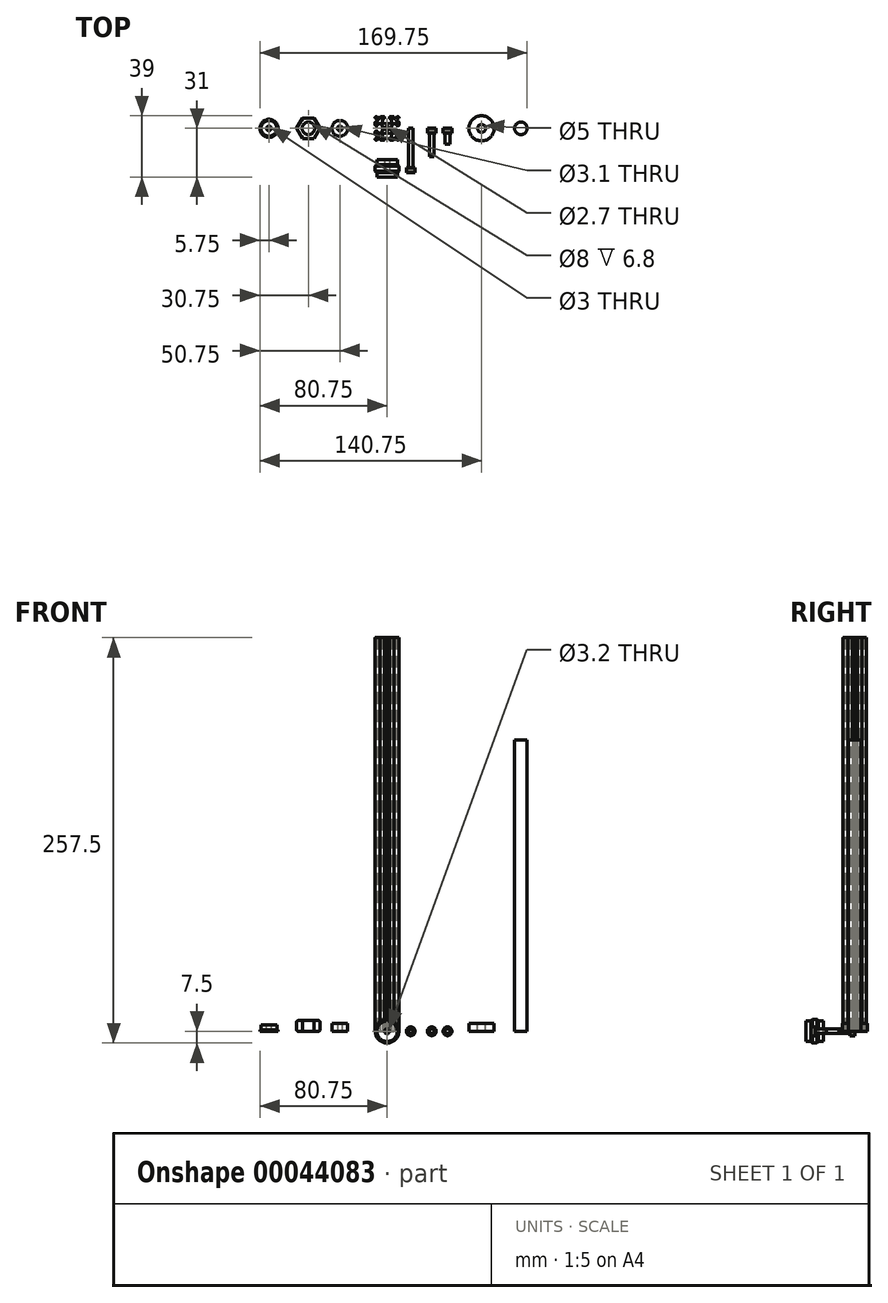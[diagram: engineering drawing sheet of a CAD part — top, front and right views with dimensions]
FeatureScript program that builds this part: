
annotation { "Feature Type Name" : "Feature", "Feature Type Description" : "" }
export const myFeature = defineFeature(function(context is Context, id is Id, definition is map)
    precondition{}
    {
        {
            var Q0;
            Q0=qCreatedBy(makeId("Top.planeOp"),FACE);
            var sketch = newSketch(context, id + "F0", { "sketchPlane" : qUnion([Q0])});
            skLineSegment(sketch, "E0", {"start": v(0, 0) * mm, "end": v(-7.5, -7.5) * mm, "construction": true});
            skArc(sketch, "E1", {"start": v(-1.35, 0) * mm, "mid": v(-1.25, -0.52) * mm, "end": v(-0.95, -0.95) * mm});
            skLineSegment(sketch, "E2", {"start": v(-7.5, -7) * mm, "end": v(-7.5, -6.72) * mm});
            skLineSegment(sketch, "E3", {"start": v(-7.35, -6.36) * mm, "end": v(-6.25, -5.26) * mm});
            skLineSegment(sketch, "E4", {"start": v(-6.6, -4.4) * mm, "end": v(-7, -4.4) * mm});
            skLineSegment(sketch, "E5", {"start": v(-7.5, -3.9) * mm, "end": v(-7.5, -2.1) * mm});
            skLineSegment(sketch, "E6", {"start": v(-7, -1.6) * mm, "end": v(-6.6, -1.6) * mm});
            skLineSegment(sketch, "E7", {"start": v(-6.1, -2.1) * mm, "end": v(-6.1, -2.7) * mm});
            skLineSegment(sketch, "E8", {"start": v(-5.9, -2.9) * mm, "end": v(-3.74, -2.9) * mm});
            skLineSegment(sketch, "E9", {"start": v(-3.25, -2.49) * mm, "end": v(-2.93, -0.73) * mm});
            skLineSegment(sketch, "E10", {"start": v(-2.73, -0.57) * mm, "end": v(-2.6, -0.57) * mm});
            skLineSegment(sketch, "E11", {"start": v(-2.4, -0.37) * mm, "end": v(-2.4, 0) * mm});
            skLineSegment(sketch, "E12", {"start": v(-2.4, 0) * mm, "end": v(-1.35, 0) * mm, "construction": true});
            skPoint(sketch, "E13.visualSharp", {"position": v(-5.4, -4.4) * mm});
            skArc(sketch, "E13.filletArc", {"start": v(-6.25, -5.26) * mm, "mid": v(-6.14, -4.71) * mm, "end": v(-6.6, -4.4) * mm});
            skPoint(sketch, "E14.visualSharp", {"position": v(-6.1, -2.9) * mm});
            skArc(sketch, "E14.filletArc", {"start": v(-6.1, -2.7) * mm, "mid": v(-6.04, -2.84) * mm, "end": v(-5.9, -2.9) * mm});
            skPoint(sketch, "E15.visualSharp", {"position": v(-6.1, -1.6) * mm});
            skArc(sketch, "E15.filletArc", {"start": v(-6.1, -2.1) * mm, "mid": v(-6.25, -1.75) * mm, "end": v(-6.6, -1.6) * mm});
            skPoint(sketch, "E16.visualSharp", {"position": v(-7.5, -1.6) * mm});
            skArc(sketch, "E16.filletArc", {"start": v(-7, -1.6) * mm, "mid": v(-7.35, -1.75) * mm, "end": v(-7.5, -2.1) * mm});
            skPoint(sketch, "E17.visualSharp", {"position": v(-7.5, -4.4) * mm});
            skArc(sketch, "E17.filletArc", {"start": v(-7.5, -3.9) * mm, "mid": v(-7.35, -4.26) * mm, "end": v(-7, -4.4) * mm});
            skPoint(sketch, "E18.visualSharp", {"position": v(-7.5, -6.51) * mm});
            skArc(sketch, "E18.filletArc", {"start": v(-7.35, -6.36) * mm, "mid": v(-7.46, -6.53) * mm, "end": v(-7.5, -6.72) * mm});
            skPoint(sketch, "E19.visualSharp", {"position": v(-3.32, -2.9) * mm});
            skArc(sketch, "E19.filletArc", {"start": v(-3.74, -2.9) * mm, "mid": v(-3.42, -2.78) * mm, "end": v(-3.25, -2.49) * mm});
            skPoint(sketch, "E20.visualSharp", {"position": v(-2.9, -0.57) * mm});
            skArc(sketch, "E20.filletArc", {"start": v(-2.73, -0.57) * mm, "mid": v(-2.86, -0.62) * mm, "end": v(-2.93, -0.73) * mm});
            skPoint(sketch, "E21.visualSharp", {"position": v(-2.4, -0.57) * mm});
            skArc(sketch, "E21.filletArc", {"start": v(-2.6, -0.57) * mm, "mid": v(-2.46, -0.51) * mm, "end": v(-2.4, -0.37) * mm});
            skLineSegment(sketch, "E22.0.MirrorCS", {"start": v(0, -2.4) * mm, "end": v(0, -1.35) * mm, "construction": true});
            skPoint(sketch, "E22.1.MirrorP", {"position": v(-4.4, -7.5) * mm});
            skArc(sketch, "E22.2.MirrorCS", {"start": v(-6.36, -7.35) * mm, "mid": v(-6.53, -7.46) * mm, "end": v(-6.72, -7.5) * mm});
            skPoint(sketch, "E22.3.MirrorP", {"position": v(-1.6, -7.5) * mm});
            skArc(sketch, "E22.4.MirrorCS", {"start": v(-1.6, -7) * mm, "mid": v(-1.75, -7.35) * mm, "end": v(-2.1, -7.5) * mm});
            skArc(sketch, "E22.5.MirrorCS", {"start": v(-0.57, -2.73) * mm, "mid": v(-0.62, -2.86) * mm, "end": v(-0.73, -2.93) * mm});
            skPoint(sketch, "E22.6.MirrorP", {"position": v(-1.6, -6.1) * mm});
            skLineSegment(sketch, "E22.7.MirrorCS", {"start": v(-3.9, -7.5) * mm, "end": v(-2.1, -7.5) * mm});
            skArc(sketch, "E22.8.MirrorCS", {"start": v(-5.26, -6.25) * mm, "mid": v(-4.71, -6.14) * mm, "end": v(-4.4, -6.6) * mm});
            skPoint(sketch, "E22.9.MirrorP", {"position": v(-0.57, -2.4) * mm});
            skPoint(sketch, "E22.10.MirrorP", {"position": v(-4.4, -5.4) * mm});
            skArc(sketch, "E22.11.MirrorCS", {"start": v(-2.7, -6.1) * mm, "mid": v(-2.84, -6.04) * mm, "end": v(-2.9, -5.9) * mm});
            skPoint(sketch, "E22.12.MirrorP", {"position": v(-0.57, -2.9) * mm});
            skLineSegment(sketch, "E22.13.MirrorCS", {"start": v(-7, -7.5) * mm, "end": v(-6.72, -7.5) * mm});
            skLineSegment(sketch, "E22.14.MirrorCS", {"start": v(-1.6, -7) * mm, "end": v(-1.6, -6.6) * mm});
            skLineSegment(sketch, "E22.15.MirrorCS", {"start": v(-6.36, -7.35) * mm, "end": v(-5.26, -6.25) * mm});
            skArc(sketch, "E22.16.MirrorCS", {"start": v(-2.1, -6.1) * mm, "mid": v(-1.75, -6.25) * mm, "end": v(-1.6, -6.6) * mm});
            skLineSegment(sketch, "E22.17.MirrorCS", {"start": v(-4.4, -6.6) * mm, "end": v(-4.4, -7) * mm});
            skArc(sketch, "E22.18.MirrorCS", {"start": v(-2.9, -3.74) * mm, "mid": v(-2.78, -3.42) * mm, "end": v(-2.49, -3.25) * mm});
            skLineSegment(sketch, "E22.19.MirrorCS", {"start": v(-2.9, -5.9) * mm, "end": v(-2.9, -3.74) * mm});
            skLineSegment(sketch, "E22.20.MirrorCS", {"start": v(-2.1, -6.1) * mm, "end": v(-2.7, -6.1) * mm});
            skArc(sketch, "E22.21.MirrorCS", {"start": v(-0.57, -2.6) * mm, "mid": v(-0.51, -2.46) * mm, "end": v(-0.37, -2.4) * mm});
            skLineSegment(sketch, "E22.22.MirrorCS", {"start": v(-0.37, -2.4) * mm, "end": v(0, -2.4) * mm});
            skPoint(sketch, "E22.23.MirrorP", {"position": v(-6.51, -7.5) * mm});
            skPoint(sketch, "E22.24.MirrorP", {"position": v(-2.9, -6.1) * mm});
            skLineSegment(sketch, "E22.25.MirrorCS", {"start": v(-2.49, -3.25) * mm, "end": v(-0.73, -2.93) * mm});
            skLineSegment(sketch, "E22.26.MirrorCS", {"start": v(-0.57, -2.73) * mm, "end": v(-0.57, -2.6) * mm});
            skArc(sketch, "E22.27.MirrorCS", {"start": v(0, -1.35) * mm, "mid": v(-0.52, -1.25) * mm, "end": v(-0.95, -0.95) * mm});
            skArc(sketch, "E22.28.MirrorCS", {"start": v(-3.9, -7.5) * mm, "mid": v(-4.26, -7.35) * mm, "end": v(-4.4, -7) * mm});
            skPoint(sketch, "E22.29.MirrorP", {"position": v(-2.9, -3.32) * mm});
            skPoint(sketch, "E23.visualSharp", {"position": v(-7.5, -7.5) * mm});
            skArc(sketch, "E23.filletArc", {"start": v(-7.5, -7) * mm, "mid": v(-7.35, -7.35) * mm, "end": v(-7, -7.5) * mm});
            skLineSegment(sketch, "E24.0.MirrorCS", {"start": v(0, 2.4) * mm, "end": v(0, 1.35) * mm, "construction": true});
            skLineSegment(sketch, "E24.1.MirrorCS", {"start": v(-2.1, 6.1) * mm, "end": v(-2.7, 6.1) * mm});
            skLineSegment(sketch, "E24.2.MirrorCS", {"start": v(-7.5, 3.9) * mm, "end": v(-7.5, 2.1) * mm});
            skLineSegment(sketch, "E24.3.MirrorCS", {"start": v(-7, 1.6) * mm, "end": v(-6.6, 1.6) * mm});
            skArc(sketch, "E24.4.MirrorCS", {"start": v(-6.1, 2.1) * mm, "mid": v(-6.25, 1.75) * mm, "end": v(-6.6, 1.6) * mm});
            skPoint(sketch, "E24.5.MirrorP", {"position": v(-3.32, 2.9) * mm});
            skPoint(sketch, "E24.6.MirrorP", {"position": v(-0.57, 2.9) * mm});
            skArc(sketch, "E24.7.MirrorCS", {"start": v(-0.57, 2.6) * mm, "mid": v(-0.51, 2.46) * mm, "end": v(-0.37, 2.4) * mm});
            skArc(sketch, "E24.8.MirrorCS", {"start": v(-2.6, 0.57) * mm, "mid": v(-2.46, 0.51) * mm, "end": v(-2.4, 0.37) * mm});
            skLineSegment(sketch, "E24.9.MirrorCS", {"start": v(-0.37, 2.4) * mm, "end": v(0, 2.4) * mm});
            skArc(sketch, "E24.10.MirrorCS", {"start": v(-6.1, 2.7) * mm, "mid": v(-6.04, 2.84) * mm, "end": v(-5.9, 2.9) * mm});
            skPoint(sketch, "E24.11.MirrorP", {"position": v(-4.4, 5.4) * mm});
            skLineSegment(sketch, "E24.12.MirrorCS", {"start": v(-2.9, 5.9) * mm, "end": v(-2.9, 3.74) * mm});
            skLineSegment(sketch, "E24.13.MirrorCS", {"start": v(-7.35, 6.36) * mm, "end": v(-6.25, 5.26) * mm});
            skPoint(sketch, "E24.14.MirrorP", {"position": v(-7.5, 6.51) * mm});
            skArc(sketch, "E24.15.MirrorCS", {"start": v(-3.74, 2.9) * mm, "mid": v(-3.42, 2.78) * mm, "end": v(-3.25, 2.49) * mm});
            skArc(sketch, "E24.16.MirrorCS", {"start": v(-2.1, 6.1) * mm, "mid": v(-1.75, 6.25) * mm, "end": v(-1.6, 6.6) * mm});
            skArc(sketch, "E24.17.MirrorCS", {"start": v(-7, 1.6) * mm, "mid": v(-7.35, 1.75) * mm, "end": v(-7.5, 2.1) * mm});
            skPoint(sketch, "E24.18.MirrorP", {"position": v(-1.6, 6.1) * mm});
            skPoint(sketch, "E24.19.MirrorP", {"position": v(-7.5, 4.4) * mm});
            skLineSegment(sketch, "E24.20.MirrorCS", {"start": v(-4.4, 6.6) * mm, "end": v(-4.4, 7) * mm});
            skArc(sketch, "E24.21.MirrorCS", {"start": v(-7.5, 3.9) * mm, "mid": v(-7.35, 4.26) * mm, "end": v(-7, 4.4) * mm});
            skPoint(sketch, "E24.22.MirrorP", {"position": v(-0.57, 2.4) * mm});
            skLineSegment(sketch, "E24.23.MirrorCS", {"start": v(-5.9, 2.9) * mm, "end": v(-3.74, 2.9) * mm});
            skArc(sketch, "E24.24.MirrorCS", {"start": v(-2.9, 3.74) * mm, "mid": v(-2.78, 3.42) * mm, "end": v(-2.49, 3.25) * mm});
            skArc(sketch, "E24.25.MirrorCS", {"start": v(-7.35, 6.36) * mm, "mid": v(-7.46, 6.53) * mm, "end": v(-7.5, 6.72) * mm});
            skPoint(sketch, "E24.26.MirrorP", {"position": v(-6.1, 2.9) * mm});
            skPoint(sketch, "E24.27.MirrorP", {"position": v(-4.4, 7.5) * mm});
            skArc(sketch, "E24.28.MirrorCS", {"start": v(-5.26, 6.25) * mm, "mid": v(-4.71, 6.14) * mm, "end": v(-4.4, 6.6) * mm});
            skArc(sketch, "E24.29.MirrorCS", {"start": v(-7.5, 7) * mm, "mid": v(-7.35, 7.35) * mm, "end": v(-7, 7.5) * mm});
            skPoint(sketch, "E24.30.MirrorP", {"position": v(-6.1, 1.6) * mm});
            skPoint(sketch, "E24.31.MirrorP", {"position": v(-2.9, 3.32) * mm});
            skPoint(sketch, "E24.32.MirrorP", {"position": v(-1.6, 7.5) * mm});
            skPoint(sketch, "E24.33.MirrorP", {"position": v(-2.9, 6.1) * mm});
            skLineSegment(sketch, "E24.34.MirrorCS", {"start": v(-3.9, 7.5) * mm, "end": v(-2.1, 7.5) * mm});
            skLineSegment(sketch, "E24.35.MirrorCS", {"start": v(-7, 7.5) * mm, "end": v(-6.72, 7.5) * mm});
            skArc(sketch, "E24.36.MirrorCS", {"start": v(-3.9, 7.5) * mm, "mid": v(-4.26, 7.35) * mm, "end": v(-4.4, 7) * mm});
            skPoint(sketch, "E24.37.MirrorP", {"position": v(-7.5, 7.5) * mm});
            skLineSegment(sketch, "E24.38.MirrorCS", {"start": v(-1.6, 7) * mm, "end": v(-1.6, 6.6) * mm});
            skLineSegment(sketch, "E24.39.MirrorCS", {"start": v(-6.36, 7.35) * mm, "end": v(-5.26, 6.25) * mm});
            skPoint(sketch, "E24.40.MirrorP", {"position": v(-7.5, 1.6) * mm});
            skArc(sketch, "E24.41.MirrorCS", {"start": v(-2.7, 6.1) * mm, "mid": v(-2.84, 6.04) * mm, "end": v(-2.9, 5.9) * mm});
            skArc(sketch, "E24.42.MirrorCS", {"start": v(-6.36, 7.35) * mm, "mid": v(-6.53, 7.46) * mm, "end": v(-6.72, 7.5) * mm});
            skLineSegment(sketch, "E24.43.MirrorCS", {"start": v(-2.49, 3.25) * mm, "end": v(-0.73, 2.93) * mm});
            skPoint(sketch, "E24.44.MirrorP", {"position": v(-2.9, 0.57) * mm});
            skLineSegment(sketch, "E24.45.MirrorCS", {"start": v(-6.6, 4.4) * mm, "end": v(-7, 4.4) * mm});
            skArc(sketch, "E24.46.MirrorCS", {"start": v(-1.6, 7) * mm, "mid": v(-1.75, 7.35) * mm, "end": v(-2.1, 7.5) * mm});
            skArc(sketch, "E24.47.MirrorCS", {"start": v(-2.73, 0.57) * mm, "mid": v(-2.86, 0.62) * mm, "end": v(-2.93, 0.73) * mm});
            skArc(sketch, "E24.48.MirrorCS", {"start": v(-6.25, 5.26) * mm, "mid": v(-6.14, 4.71) * mm, "end": v(-6.6, 4.4) * mm});
            skLineSegment(sketch, "E24.49.MirrorCS", {"start": v(-0.57, 2.73) * mm, "end": v(-0.57, 2.6) * mm});
            skLineSegment(sketch, "E24.50.MirrorCS", {"start": v(-2.73, 0.57) * mm, "end": v(-2.6, 0.57) * mm});
            skArc(sketch, "E24.51.MirrorCS", {"start": v(-1.35, 0) * mm, "mid": v(-1.25, 0.52) * mm, "end": v(-0.95, 0.95) * mm});
            skPoint(sketch, "E24.52.MirrorP", {"position": v(-2.4, 0.57) * mm});
            skPoint(sketch, "E24.53.MirrorP", {"position": v(-5.4, 4.4) * mm});
            skLineSegment(sketch, "E24.54.MirrorCS", {"start": v(-2.4, 0.37) * mm, "end": v(-2.4, 0) * mm});
            skArc(sketch, "E24.55.MirrorCS", {"start": v(0, 1.35) * mm, "mid": v(-0.52, 1.25) * mm, "end": v(-0.95, 0.95) * mm});
            skLineSegment(sketch, "E24.56.MirrorCS", {"start": v(-3.25, 2.49) * mm, "end": v(-2.93, 0.73) * mm});
            skLineSegment(sketch, "E24.57.MirrorCS", {"start": v(-6.1, 2.1) * mm, "end": v(-6.1, 2.7) * mm});
            skLineSegment(sketch, "E24.58.MirrorCS", {"start": v(-7.5, 7) * mm, "end": v(-7.5, 6.72) * mm});
            skArc(sketch, "E24.59.MirrorCS", {"start": v(-0.57, 2.73) * mm, "mid": v(-0.62, 2.86) * mm, "end": v(-0.73, 2.93) * mm});
            skPoint(sketch, "E24.60.MirrorP", {"position": v(-6.51, 7.5) * mm});
            skLineSegment(sketch, "E25.0.MirrorCS", {"start": v(7, -7.5) * mm, "end": v(6.72, -7.5) * mm});
            skLineSegment(sketch, "E25.1.MirrorCS", {"start": v(0.57, 2.73) * mm, "end": v(0.57, 2.6) * mm});
            skLineSegment(sketch, "E25.2.MirrorCS", {"start": v(0.37, 2.4) * mm, "end": v(0, 2.4) * mm});
            skLineSegment(sketch, "E25.3.MirrorCS", {"start": v(7, 7.5) * mm, "end": v(6.72, 7.5) * mm});
            skLineSegment(sketch, "E25.4.MirrorCS", {"start": v(1.6, -7) * mm, "end": v(1.6, -6.6) * mm});
            skLineSegment(sketch, "E25.5.MirrorCS", {"start": v(2.73, 0.57) * mm, "end": v(2.6, 0.57) * mm});
            skLineSegment(sketch, "E25.6.MirrorCS", {"start": v(7, 1.6) * mm, "end": v(6.6, 1.6) * mm});
            skLineSegment(sketch, "E25.7.MirrorCS", {"start": v(5.9, 2.9) * mm, "end": v(3.74, 2.9) * mm});
            skLineSegment(sketch, "E25.8.MirrorCS", {"start": v(7.35, 6.36) * mm, "end": v(6.25, 5.26) * mm});
            skArc(sketch, "E25.9.MirrorCS", {"start": v(2.7, -6.1) * mm, "mid": v(2.84, -6.04) * mm, "end": v(2.9, -5.9) * mm});
            skArc(sketch, "E25.10.MirrorCS", {"start": v(2.9, 3.74) * mm, "mid": v(2.78, 3.42) * mm, "end": v(2.49, 3.25) * mm});
            skPoint(sketch, "E25.11.MirrorP", {"position": v(1.6, -7.5) * mm});
            skPoint(sketch, "E25.12.MirrorP", {"position": v(6.1, -1.6) * mm});
            skPoint(sketch, "E25.13.MirrorP", {"position": v(2.9, 3.32) * mm});
            skPoint(sketch, "E25.14.MirrorP", {"position": v(7.5, -1.6) * mm});
            skArc(sketch, "E25.15.MirrorCS", {"start": v(1.6, 7) * mm, "mid": v(1.75, 7.35) * mm, "end": v(2.1, 7.5) * mm});
            skLineSegment(sketch, "E25.16.MirrorCS", {"start": v(6.1, -2.1) * mm, "end": v(6.1, -2.7) * mm});
            skLineSegment(sketch, "E25.17.MirrorCS", {"start": v(2.4, 0.37) * mm, "end": v(2.4, 0) * mm});
            skArc(sketch, "E25.18.MirrorCS", {"start": v(7, -1.6) * mm, "mid": v(7.35, -1.75) * mm, "end": v(7.5, -2.1) * mm});
            skArc(sketch, "E25.19.MirrorCS", {"start": v(7.5, 7) * mm, "mid": v(7.35, 7.35) * mm, "end": v(7, 7.5) * mm});
            skArc(sketch, "E25.20.MirrorCS", {"start": v(2.1, -6.1) * mm, "mid": v(1.75, -6.25) * mm, "end": v(1.6, -6.6) * mm});
            skArc(sketch, "E25.21.MirrorCS", {"start": v(6.1, 2.1) * mm, "mid": v(6.25, 1.75) * mm, "end": v(6.6, 1.6) * mm});
            skLineSegment(sketch, "E25.22.MirrorCS", {"start": v(4.4, 6.6) * mm, "end": v(4.4, 7) * mm});
            skLineSegment(sketch, "E25.23.MirrorCS", {"start": v(6.6, 4.4) * mm, "end": v(7, 4.4) * mm});
            skArc(sketch, "E25.24.MirrorCS", {"start": v(7, 1.6) * mm, "mid": v(7.35, 1.75) * mm, "end": v(7.5, 2.1) * mm});
            skArc(sketch, "E25.25.MirrorCS", {"start": v(0, -1.35) * mm, "mid": v(0.52, -1.25) * mm, "end": v(0.95, -0.95) * mm});
            skLineSegment(sketch, "E25.26.MirrorCS", {"start": v(3.9, -7.5) * mm, "end": v(2.1, -7.5) * mm});
            skLineSegment(sketch, "E25.27.MirrorCS", {"start": v(2.1, 6.1) * mm, "end": v(2.7, 6.1) * mm});
            skLineSegment(sketch, "E25.28.MirrorCS", {"start": v(2.73, -0.57) * mm, "end": v(2.6, -0.57) * mm});
            skLineSegment(sketch, "E25.29.MirrorCS", {"start": v(4.4, -6.6) * mm, "end": v(4.4, -7) * mm});
            skLineSegment(sketch, "E25.30.MirrorCS", {"start": v(3.9, 7.5) * mm, "end": v(2.1, 7.5) * mm});
            skArc(sketch, "E25.31.MirrorCS", {"start": v(0.57, -2.73) * mm, "mid": v(0.62, -2.86) * mm, "end": v(0.73, -2.93) * mm});
            skArc(sketch, "E25.32.MirrorCS", {"start": v(0.57, 2.6) * mm, "mid": v(0.51, 2.46) * mm, "end": v(0.37, 2.4) * mm});
            skPoint(sketch, "E25.33.MirrorP", {"position": v(6.51, -7.5) * mm});
            skArc(sketch, "E25.34.MirrorCS", {"start": v(3.9, -7.5) * mm, "mid": v(4.26, -7.35) * mm, "end": v(4.4, -7) * mm});
            skArc(sketch, "E25.35.MirrorCS", {"start": v(2.7, 6.1) * mm, "mid": v(2.84, 6.04) * mm, "end": v(2.9, 5.9) * mm});
            skPoint(sketch, "E25.36.MirrorP", {"position": v(0.57, -2.4) * mm});
            skPoint(sketch, "E25.37.MirrorP", {"position": v(0.57, 2.9) * mm});
            skLineSegment(sketch, "E25.38.MirrorCS", {"start": v(3.25, -2.49) * mm, "end": v(2.93, -0.73) * mm});
            skPoint(sketch, "E25.39.MirrorP", {"position": v(5.4, -4.4) * mm});
            skPoint(sketch, "E25.40.MirrorP", {"position": v(2.4, -0.57) * mm});
            skLineSegment(sketch, "E25.41.MirrorCS", {"start": v(7.5, -7) * mm, "end": v(7.5, -6.72) * mm});
            skArc(sketch, "E25.42.MirrorCS", {"start": v(7.35, 6.36) * mm, "mid": v(7.46, 6.53) * mm, "end": v(7.5, 6.72) * mm});
            skPoint(sketch, "E25.43.MirrorP", {"position": v(4.4, 7.5) * mm});
            skArc(sketch, "E25.44.MirrorCS", {"start": v(6.25, 5.26) * mm, "mid": v(6.14, 4.71) * mm, "end": v(6.6, 4.4) * mm});
            skPoint(sketch, "E25.45.MirrorP", {"position": v(6.1, -2.9) * mm});
            skPoint(sketch, "E25.46.MirrorP", {"position": v(4.4, -7.5) * mm});
            skArc(sketch, "E25.47.MirrorCS", {"start": v(6.1, 2.7) * mm, "mid": v(6.04, 2.84) * mm, "end": v(5.9, 2.9) * mm});
            skLineSegment(sketch, "E25.48.MirrorCS", {"start": v(2.1, -6.1) * mm, "end": v(2.7, -6.1) * mm});
            skArc(sketch, "E25.49.MirrorCS", {"start": v(2.73, -0.57) * mm, "mid": v(2.86, -0.62) * mm, "end": v(2.93, -0.73) * mm});
            skArc(sketch, "E25.50.MirrorCS", {"start": v(7.35, -6.36) * mm, "mid": v(7.46, -6.53) * mm, "end": v(7.5, -6.72) * mm});
            skLineSegment(sketch, "E25.51.MirrorCS", {"start": v(3.25, 2.49) * mm, "end": v(2.93, 0.73) * mm});
            skArc(sketch, "E25.52.MirrorCS", {"start": v(2.9, -3.74) * mm, "mid": v(2.78, -3.42) * mm, "end": v(2.49, -3.25) * mm});
            skArc(sketch, "E25.53.MirrorCS", {"start": v(2.6, 0.57) * mm, "mid": v(2.46, 0.51) * mm, "end": v(2.4, 0.37) * mm});
            skPoint(sketch, "E25.54.MirrorP", {"position": v(2.9, 0.57) * mm});
            skPoint(sketch, "E25.55.MirrorP", {"position": v(7.5, -6.51) * mm});
            skLineSegment(sketch, "E25.56.MirrorCS", {"start": v(2.49, 3.25) * mm, "end": v(0.73, 2.93) * mm});
            skArc(sketch, "E25.57.MirrorCS", {"start": v(1.6, -7) * mm, "mid": v(1.75, -7.35) * mm, "end": v(2.1, -7.5) * mm});
            skArc(sketch, "E25.58.MirrorCS", {"start": v(2.1, 6.1) * mm, "mid": v(1.75, 6.25) * mm, "end": v(1.6, 6.6) * mm});
            skLineSegment(sketch, "E25.59.MirrorCS", {"start": v(0.57, -2.73) * mm, "end": v(0.57, -2.6) * mm});
            skLineSegment(sketch, "E25.60.MirrorCS", {"start": v(2.4, -0.37) * mm, "end": v(2.4, 0) * mm});
            skArc(sketch, "E25.61.MirrorCS", {"start": v(7.5, -3.9) * mm, "mid": v(7.35, -4.26) * mm, "end": v(7, -4.4) * mm});
            skLineSegment(sketch, "E25.62.MirrorCS", {"start": v(5.9, -2.9) * mm, "end": v(3.74, -2.9) * mm});
            skLineSegment(sketch, "E25.63.MirrorCS", {"start": v(7.5, -3.9) * mm, "end": v(7.5, -2.1) * mm});
            skLineSegment(sketch, "E25.64.MirrorCS", {"start": v(7, -1.6) * mm, "end": v(6.6, -1.6) * mm});
            skArc(sketch, "E25.65.MirrorCS", {"start": v(1.35, 0) * mm, "mid": v(1.25, -0.52) * mm, "end": v(0.95, -0.95) * mm});
            skPoint(sketch, "E25.66.MirrorP", {"position": v(7.5, 1.6) * mm});
            skPoint(sketch, "E25.67.MirrorP", {"position": v(1.6, 6.1) * mm});
            skLineSegment(sketch, "E25.68.MirrorCS", {"start": v(6.36, -7.35) * mm, "end": v(5.26, -6.25) * mm});
            skPoint(sketch, "E25.69.MirrorP", {"position": v(2.4, 0.57) * mm});
            skPoint(sketch, "E25.70.MirrorP", {"position": v(6.1, 1.6) * mm});
            skPoint(sketch, "E25.71.MirrorP", {"position": v(3.32, -2.9) * mm});
            skPoint(sketch, "E25.72.MirrorP", {"position": v(0.57, -2.9) * mm});
            skPoint(sketch, "E25.73.MirrorP", {"position": v(7.5, 4.4) * mm});
            skArc(sketch, "E25.74.MirrorCS", {"start": v(5.26, -6.25) * mm, "mid": v(4.71, -6.14) * mm, "end": v(4.4, -6.6) * mm});
            skArc(sketch, "E25.75.MirrorCS", {"start": v(7.5, -7) * mm, "mid": v(7.35, -7.35) * mm, "end": v(7, -7.5) * mm});
            skLineSegment(sketch, "E25.76.MirrorCS", {"start": v(2.49, -3.25) * mm, "end": v(0.73, -2.93) * mm});
            skArc(sketch, "E25.77.MirrorCS", {"start": v(3.74, 2.9) * mm, "mid": v(3.42, 2.78) * mm, "end": v(3.25, 2.49) * mm});
            skArc(sketch, "E25.78.MirrorCS", {"start": v(6.36, -7.35) * mm, "mid": v(6.53, -7.46) * mm, "end": v(6.72, -7.5) * mm});
            skArc(sketch, "E25.79.MirrorCS", {"start": v(7.5, 3.9) * mm, "mid": v(7.35, 4.26) * mm, "end": v(7, 4.4) * mm});
            skArc(sketch, "E25.80.MirrorCS", {"start": v(2.73, 0.57) * mm, "mid": v(2.86, 0.62) * mm, "end": v(2.93, 0.73) * mm});
            skArc(sketch, "E25.81.MirrorCS", {"start": v(6.36, 7.35) * mm, "mid": v(6.53, 7.46) * mm, "end": v(6.72, 7.5) * mm});
            skPoint(sketch, "E25.82.MirrorP", {"position": v(4.4, -5.4) * mm});
            skPoint(sketch, "E25.83.MirrorP", {"position": v(6.51, 7.5) * mm});
            skPoint(sketch, "E25.84.MirrorP", {"position": v(2.9, -0.57) * mm});
            skLineSegment(sketch, "E25.85.MirrorCS", {"start": v(2.9, -5.9) * mm, "end": v(2.9, -3.74) * mm});
            skLineSegment(sketch, "E25.86.MirrorCS", {"start": v(6.1, 2.1) * mm, "end": v(6.1, 2.7) * mm});
            skLineSegment(sketch, "E25.87.MirrorCS", {"start": v(6.36, 7.35) * mm, "end": v(5.26, 6.25) * mm});
            skArc(sketch, "E25.88.MirrorCS", {"start": v(0.57, 2.73) * mm, "mid": v(0.62, 2.86) * mm, "end": v(0.73, 2.93) * mm});
            skArc(sketch, "E25.89.MirrorCS", {"start": v(0.57, -2.6) * mm, "mid": v(0.51, -2.46) * mm, "end": v(0.37, -2.4) * mm});
            skLineSegment(sketch, "E25.90.MirrorCS", {"start": v(2.9, 5.9) * mm, "end": v(2.9, 3.74) * mm});
            skArc(sketch, "E25.91.MirrorCS", {"start": v(0, 1.35) * mm, "mid": v(0.52, 1.25) * mm, "end": v(0.95, 0.95) * mm});
            skArc(sketch, "E25.92.MirrorCS", {"start": v(2.6, -0.57) * mm, "mid": v(2.46, -0.51) * mm, "end": v(2.4, -0.37) * mm});
            skPoint(sketch, "E25.93.MirrorP", {"position": v(4.4, 5.4) * mm});
            skPoint(sketch, "E25.94.MirrorP", {"position": v(2.9, -3.32) * mm});
            skPoint(sketch, "E25.95.MirrorP", {"position": v(2.9, 6.1) * mm});
            skPoint(sketch, "E25.96.MirrorP", {"position": v(5.4, 4.4) * mm});
            skPoint(sketch, "E25.97.MirrorP", {"position": v(3.32, 2.9) * mm});
            skArc(sketch, "E25.98.MirrorCS", {"start": v(3.74, -2.9) * mm, "mid": v(3.42, -2.78) * mm, "end": v(3.25, -2.49) * mm});
            skArc(sketch, "E25.99.MirrorCS", {"start": v(3.9, 7.5) * mm, "mid": v(4.26, 7.35) * mm, "end": v(4.4, 7) * mm});
            skPoint(sketch, "E25.100.MirrorP", {"position": v(7.5, -4.4) * mm});
            skPoint(sketch, "E25.101.MirrorP", {"position": v(6.1, 2.9) * mm});
            skArc(sketch, "E25.102.MirrorCS", {"start": v(1.35, 0) * mm, "mid": v(1.25, 0.52) * mm, "end": v(0.95, 0.95) * mm});
            skArc(sketch, "E25.103.MirrorCS", {"start": v(5.26, 6.25) * mm, "mid": v(4.71, 6.14) * mm, "end": v(4.4, 6.6) * mm});
            skPoint(sketch, "E25.104.MirrorP", {"position": v(7.5, 6.51) * mm});
            skPoint(sketch, "E25.105.MirrorP", {"position": v(2.9, -6.1) * mm});
            skArc(sketch, "E25.106.MirrorCS", {"start": v(6.25, -5.26) * mm, "mid": v(6.14, -4.71) * mm, "end": v(6.6, -4.4) * mm});
            skArc(sketch, "E25.107.MirrorCS", {"start": v(6.1, -2.1) * mm, "mid": v(6.25, -1.75) * mm, "end": v(6.6, -1.6) * mm});
            skPoint(sketch, "E25.108.MirrorP", {"position": v(1.6, 7.5) * mm});
            skPoint(sketch, "E25.109.MirrorP", {"position": v(7.5, 7.5) * mm});
            skLineSegment(sketch, "E25.110.MirrorCS", {"start": v(0.37, -2.4) * mm, "end": v(0, -2.4) * mm});
            skPoint(sketch, "E25.111.MirrorP", {"position": v(7.5, -7.5) * mm});
            skLineSegment(sketch, "E25.112.MirrorCS", {"start": v(7.5, 7) * mm, "end": v(7.5, 6.72) * mm});
            skArc(sketch, "E25.113.MirrorCS", {"start": v(6.1, -2.7) * mm, "mid": v(6.04, -2.84) * mm, "end": v(5.9, -2.9) * mm});
            skLineSegment(sketch, "E25.114.MirrorCS", {"start": v(1.6, 7) * mm, "end": v(1.6, 6.6) * mm});
            skPoint(sketch, "E25.115.MirrorP", {"position": v(1.6, -6.1) * mm});
            skLineSegment(sketch, "E25.116.MirrorCS", {"start": v(7.35, -6.36) * mm, "end": v(6.25, -5.26) * mm});
            skLineSegment(sketch, "E25.117.MirrorCS", {"start": v(7.5, 3.9) * mm, "end": v(7.5, 2.1) * mm});
            skPoint(sketch, "E25.118.MirrorP", {"position": v(0.57, 2.4) * mm});
            skLineSegment(sketch, "E25.119.MirrorCS", {"start": v(6.6, -4.4) * mm, "end": v(7, -4.4) * mm});
            skSolve(sketch);
        }
        {
            var Q0;
            Q0=makeQuery(id+"F0.imprint","IMPRINT",FACE,{"disambiguationData":[TD([[makeQuery(id+"F0.imprint","IMPRINT",EDGE,{"derivedFrom":sQuery(id+"F0.wireOp",EDGE,"E1")}),-1.0]])]});
            extrude(context, id + "F1", {"entities" : qUnion([Q0]), "depth" : 250 * mm});
        }
        {
            var Q0;
            Q0=qCreatedBy(makeId("Right.planeOp"),FACE);
            var sketch = newSketch(context, id + "F2", { "sketchPlane" : qUnion([Q0])});
            skLineSegment(sketch, "E26", {"start": v(-31, 0) * mm, "end": v(-31, 6.5) * mm});
            skLineSegment(sketch, "E27", {"start": v(-20, 6.5) * mm, "end": v(-20, 0) * mm});
            skLineSegment(sketch, "E28", {"start": v(-20, 0) * mm, "end": v(-31, 0) * mm});
            skLineSegment(sketch, "E29", {"start": v(-31, 6.5) * mm, "end": v(-28, 6.5) * mm});
            skLineSegment(sketch, "E30", {"start": v(-28, 6.5) * mm, "end": v(-27, 7.5) * mm});
            skLineSegment(sketch, "E31", {"start": v(-27, 7.5) * mm, "end": v(-24, 7.5) * mm});
            skLineSegment(sketch, "E32", {"start": v(-24, 7.5) * mm, "end": v(-23, 6.5) * mm});
            skLineSegment(sketch, "E33", {"start": v(-23, 6.5) * mm, "end": v(-20, 6.5) * mm});
            skLineSegment(sketch, "E34", {"start": v(-25.5, 7.5) * mm, "end": v(-25.5, 0) * mm, "construction": true});
            skSolve(sketch);
        }
        {
            var Q0;
            Q0 = qSketchRegion(id + "F2", true);
            var Q1;
            Q1=sQuery(id+"F2.wireOp",EDGE,"E28");
            revolve(context, id + "F3", {"entities" : qUnion([Q0]), "axis" : qUnion([Q1]), "revolveType" : RevolveType.FULL});
        }
        {
            var Q0;
            Q0=makeQuery(id+"F3.opRevolve","SWEPT_FACE",FACE,{"disambiguationData":[OSD([sQuery(id+"F2.wireOp",EDGE,"E26")])]});
            var sketch = newSketch(context, id + "F4", { "sketchPlane" : qUnion([Q0])});
            skCircle(sketch, "E35", {"center": v(0, 0) * mm, "radius": 1.6 * mm});
            skSolve(sketch);
        }
        {
            var Q0;
            Q0=makeQuery(id+"F4.imprint","IMPRINT",FACE,{"disambiguationData":[TD([[makeQuery(id+"F4.imprint","IMPRINT",EDGE,{"derivedFrom":sQuery(id+"F4.wireOp",EDGE,"E35")}),1.0]])]});
            extrude(context, id + "F5", {"entities" : qUnion([Q0]), "operationType" : NewBodyOperationType.REMOVE, "oppositeDirection" : true, "depth" : 11 * mm});
        }
        {
            var Q0;
            Q0=qCreatedBy(makeId("Front.planeOp"),FACE);
            var sketch = newSketch(context, id + "F6", { "sketchPlane" : qUnion([Q0])});
            skCircle(sketch, "E36", {"center": v(15, 0) * mm, "radius": 1.5 * mm});
            skSolve(sketch);
        }
        {
            var Q0;
            Q0=makeQuery(id+"F6.imprint","IMPRINT",FACE,{"disambiguationData":[TD([[makeQuery(id+"F6.imprint","IMPRINT",EDGE,{"derivedFrom":sQuery(id+"F6.wireOp",EDGE,"E36")}),1.0]])]});
            extrude(context, id + "F7", {"entities" : qUnion([Q0]), "depth" : 25 * mm});
        }
        {
            var Q0;
            Q0=makeQuery(id+"F7.opExtrude","CAP_FACE",FACE,{"disambiguationData":[OSD([sQuery(id+"F6.wireOp",EDGE,"E36")])],"isStart":false});
            var sketch = newSketch(context, id + "F8", { "sketchPlane" : qUnion([Q0])});
            skCircle(sketch, "E37", {"center": v(15, 0) * mm, "radius": 2.8 * mm});
            skSolve(sketch);
        }
        {
            var Q0;
            Q0=makeQuery(id+"F8.imprint","IMPRINT",FACE,{"disambiguationData":[TD([[makeQuery(id+"F8.imprint","IMPRINT",EDGE,{"derivedFrom":sQuery(id+"F8.wireOp",EDGE,"E37")}),1.0]])]});
            var Q1;
            Q1=makeQuery(id+"F8.imprint","IMPRINT",FACE,{"disambiguationData":[TD([[makeQuery(id+"F8.imprint","IMPRINT",EDGE,{"derivedFrom":makeQuery(id+"F7.opExtrude","CAP_EDGE",EDGE,{"disambiguationData":[OSD([sQuery(id+"F6.wireOp",EDGE,"E36")])],"isStart":false})}),1.0]])]});
            extrude(context, id + "F9", {"entities" : qUnion([Q0, Q1]), "operationType" : NewBodyOperationType.ADD, "depth" : 3 * mm});
        }
        {
            var Q0;
            Q0=qCreatedBy(makeId("Top.planeOp"),FACE);
            var sketch = newSketch(context, id + "F10", { "sketchPlane" : qUnion([Q0])});
            skCircle(sketch, "E38", {"center": v(-30, 0) * mm, "radius": 5 * mm});
            skCircle(sketch, "E39", {"center": v(-30, 0) * mm, "radius": 1.55 * mm});
            skSolve(sketch);
        }
        {
            var Q0;
            Q0=makeQuery(id+"F10.imprint","IMPRINT",FACE,{"disambiguationData":[TD([[makeQuery(id+"F10.imprint","IMPRINT",EDGE,{"derivedFrom":sQuery(id+"F10.wireOp",EDGE,"E38")}),1.0]])]});
            extrude(context, id + "F11", {"entities" : qUnion([Q0]), "depth" : 5 * mm});
        }
        {
            var Q0;
            Q0=makeQuery(id+"F7.opExtrude","SWEPT_BODY",BODY,{"disambiguationData":[OSD([sQuery(id+"F6.wireOp",EDGE,"E36")])]});
            transform(context, id + "F12", {"entities" : qUnion([Q0]), "transformType" : TransformType.TRANSLATION_3D, "dx" : 13.4 * mm, "dy" : 0 * mm, "dz" : 0 * mm, "makeCopy" : true});
        }
        {
            var Q0;
            Q0=makeQuery(id+"F12.opPattern","COPY",BODY,{"derivedFrom":makeQuery(id+"F7.opExtrude","SWEPT_BODY",BODY,{"disambiguationData":[OSD([sQuery(id+"F6.wireOp",EDGE,"E36")])]}),"instanceName":"1"});
            deleteBodies(context, id + "F13", {"entities" : qUnion([Q0])});
        }
        {
            var Q0;
            Q0=qCreatedBy(makeId("Front.planeOp"),FACE);
            var sketch = newSketch(context, id + "F14", { "sketchPlane" : qUnion([Q0])});
            skCircle(sketch, "E40", {"center": v(28.37, 0) * mm, "radius": 2.8 * mm});
            skSolve(sketch);
        }
        {
            var Q0;
            Q0=makeQuery(id+"F14.imprint","IMPRINT",FACE,{"disambiguationData":[TD([[makeQuery(id+"F14.imprint","IMPRINT",EDGE,{"derivedFrom":sQuery(id+"F14.wireOp",EDGE,"E40")}),1.0]])]});
            extrude(context, id + "F15", {"entities" : qUnion([Q0]), "depth" : 3 * mm});
        }
        {
            var Q0;
            Q0=makeQuery(id+"F15.opExtrude","CAP_FACE",FACE,{"disambiguationData":[OSD([sQuery(id+"F14.wireOp",EDGE,"E40")])],"isStart":false});
            var sketch = newSketch(context, id + "F16", { "sketchPlane" : qUnion([Q0])});
            skCircle(sketch, "E41", {"center": v(28.37, 0) * mm, "radius": 1.5 * mm});
            skSolve(sketch);
        }
        {
            var Q0;
            Q0=makeQuery(id+"F16.imprint","IMPRINT",FACE,{"disambiguationData":[TD([[makeQuery(id+"F16.imprint","IMPRINT",EDGE,{"derivedFrom":sQuery(id+"F16.wireOp",EDGE,"E41")}),1.0]])]});
            extrude(context, id + "F17", {"entities" : qUnion([Q0]), "operationType" : NewBodyOperationType.ADD, "depth" : 15 * mm});
        }
        {
            var Q0;
            Q0=makeQuery(id+"F9.opExtrude","CAP_FACE",FACE,{"disambiguationData":[OSD([sQuery(id+"F8.wireOp",EDGE,"E37")])],"isStart":false});
            var sketch = newSketch(context, id + "F18", { "sketchPlane" : qUnion([Q0])});
            skCircle(sketch, "E42.cCircle", {"center": v(15, 0) * mm, "radius": 1.53 * mm, "construction": true});
            skLineSegment(sketch, "E42.0", {"start": v(15.88, -1.53) * mm, "end": v(14.12, -1.53) * mm});
            skLineSegment(sketch, "E42.1", {"start": v(14.12, -1.53) * mm, "end": v(13.24, 0) * mm});
            skLineSegment(sketch, "E42.2", {"start": v(13.24, 0) * mm, "end": v(14.12, 1.53) * mm});
            skLineSegment(sketch, "E42.3", {"start": v(14.12, 1.53) * mm, "end": v(15.88, 1.53) * mm});
            skLineSegment(sketch, "E42.4", {"start": v(15.88, 1.53) * mm, "end": v(16.76, 0) * mm});
            skLineSegment(sketch, "E42.5", {"start": v(16.76, 0) * mm, "end": v(15.88, -1.53) * mm});
            skPoint(sketch, "E42.0.midPoint", {"position": v(15, -1.53) * mm});
            skSolve(sketch);
        }
        {
            var Q0;
            Q0=makeQuery(id+"F18.imprint","IMPRINT",FACE,{"disambiguationData":[TD([[makeQuery(id+"F18.imprint","IMPRINT",EDGE,{"derivedFrom":sQuery(id+"F18.wireOp",EDGE,"E42.0")}),-1.0]])]});
            extrude(context, id + "F19", {"entities" : qUnion([Q0]), "operationType" : NewBodyOperationType.REMOVE, "oppositeDirection" : true, "depth" : 1.5 * mm});
        }
        {
            var Q0;
            Q0=makeQuery(id+"F15.opExtrude","CAP_FACE",FACE,{"disambiguationData":[OSD([sQuery(id+"F14.wireOp",EDGE,"E40")])],"isStart":true});
            var sketch = newSketch(context, id + "F20", { "sketchPlane" : qUnion([Q0])});
            skCircle(sketch, "E43.cCircle", {"center": v(-28.37, 0) * mm, "radius": 1.5 * mm, "construction": true});
            skLineSegment(sketch, "E43.0", {"start": v(-27.5, -1.5) * mm, "end": v(-29.24, -1.5) * mm});
            skLineSegment(sketch, "E43.1", {"start": v(-29.24, -1.5) * mm, "end": v(-30.1, 0) * mm});
            skLineSegment(sketch, "E43.2", {"start": v(-30.1, 0) * mm, "end": v(-29.24, 1.5) * mm});
            skLineSegment(sketch, "E43.3", {"start": v(-29.24, 1.5) * mm, "end": v(-27.5, 1.5) * mm});
            skLineSegment(sketch, "E43.4", {"start": v(-27.5, 1.5) * mm, "end": v(-26.63, 0) * mm});
            skLineSegment(sketch, "E43.5", {"start": v(-26.63, 0) * mm, "end": v(-27.5, -1.5) * mm});
            skPoint(sketch, "E43.0.midPoint", {"position": v(-28.37, -1.5) * mm});
            skSolve(sketch);
        }
        {
            var Q0;
            Q0 = qSketchRegion(id + "F20", true);
            extrude(context, id + "F21", {"entities" : qUnion([Q0]), "operationType" : NewBodyOperationType.REMOVE, "oppositeDirection" : true, "depth" : 1.5 * mm});
        }
        {
            var Q0;
            Q0=makeQuery(id+"F15.opExtrude","SWEPT_BODY",BODY,{"disambiguationData":[OSD([sQuery(id+"F14.wireOp",EDGE,"E40")])]});
            transform(context, id + "F22", {"entities" : qUnion([Q0]), "transformType" : TransformType.TRANSLATION_3D, "dx" : 10 * mm, "dy" : 0 * mm, "dz" : 0 * mm, "makeCopy" : true});
        }
        {
            var Q0;
            Q0=makeQuery(id+"F22.opPattern","COPY",FACE,{"derivedFrom":makeQuery(id+"F17.opExtrude","CAP_FACE",FACE,{"disambiguationData":[OSD([sQuery(id+"F16.wireOp",EDGE,"E41")])],"isStart":false}),"instanceName":"1"});
            var sketch = newSketch(context, id + "F23", { "sketchPlane" : qUnion([Q0])});
            skCircle(sketch, "E44.0", {"center": v(38.37, 0) * mm, "radius": 1.5 * mm});
            skSolve(sketch);
        }
        {
            var Q0;
            Q0 = qSketchRegion(id + "F23", true);
            extrude(context, id + "F24", {"entities" : qUnion([Q0]), "operationType" : NewBodyOperationType.REMOVE, "oppositeDirection" : true, "depth" : 8 * mm});
        }
        {
            var Q0;
            Q0=qCreatedBy(makeId("Top.planeOp"),FACE);
            var sketch = newSketch(context, id + "F25", { "sketchPlane" : qUnion([Q0])});
            skCircle(sketch, "E45.cCircle", {"center": v(-50, 0) * mm, "radius": 6.5 * mm, "construction": true});
            skLineSegment(sketch, "E45.0", {"start": v(-46.25, -6.5) * mm, "end": v(-53.75, -6.5) * mm});
            skLineSegment(sketch, "E45.1", {"start": v(-53.75, -6.5) * mm, "end": v(-57.5, 0) * mm});
            skLineSegment(sketch, "E45.2", {"start": v(-57.5, 0) * mm, "end": v(-53.75, 6.5) * mm});
            skLineSegment(sketch, "E45.3", {"start": v(-53.75, 6.5) * mm, "end": v(-46.25, 6.5) * mm});
            skLineSegment(sketch, "E45.4", {"start": v(-46.25, 6.5) * mm, "end": v(-42.5, 0) * mm});
            skLineSegment(sketch, "E45.5", {"start": v(-42.5, 0) * mm, "end": v(-46.25, -6.5) * mm});
            skPoint(sketch, "E45.0.midPoint", {"position": v(-50, -6.5) * mm});
            skSolve(sketch);
        }
        {
            var Q0;
            Q0 = qSketchRegion(id + "F25", true);
            extrude(context, id + "F26", {"entities" : qUnion([Q0]), "depth" : 6.8 * mm});
        }
        {
            var Q0;
            Q0=makeQuery(id+"F26.opExtrude","CAP_FACE",FACE,{"disambiguationData":[OSD([sQuery(id+"F25.wireOp",EDGE,"E45.0"),sQuery(id+"F25.wireOp",EDGE,"E45.1"),sQuery(id+"F25.wireOp",EDGE,"E45.2"),sQuery(id+"F25.wireOp",EDGE,"E45.3"),sQuery(id+"F25.wireOp",EDGE,"E45.4"),sQuery(id+"F25.wireOp",EDGE,"E45.5")])],"isStart":false});
            var sketch = newSketch(context, id + "F27", { "sketchPlane" : qUnion([Q0])});
            skCircle(sketch, "E46", {"center": v(-50, 0) * mm, "radius": 4 * mm});
            skLineSegment(sketch, "E47", {"start": v(-50, 6.5) * mm, "end": v(-50, -6.5) * mm, "construction": true});
            skSolve(sketch);
        }
        {
            var Q0;
            Q0 = qSketchRegion(id + "F27", true);
            var Q1;
            Q1=makeQuery(id+"F26.opExtrude","CAP_FACE",FACE,{"disambiguationData":[OSD([sQuery(id+"F25.wireOp",EDGE,"E45.0"),sQuery(id+"F25.wireOp",EDGE,"E45.1"),sQuery(id+"F25.wireOp",EDGE,"E45.2"),sQuery(id+"F25.wireOp",EDGE,"E45.3"),sQuery(id+"F25.wireOp",EDGE,"E45.4"),sQuery(id+"F25.wireOp",EDGE,"E45.5")])],"isStart":true});
            extrude(context, id + "F28", {"entities" : qUnion([Q0, Q1]), "operationType" : NewBodyOperationType.REMOVE, "oppositeDirection" : true, "depth" : 7 * mm});
        }
        {
            var Q0;
            Q0=makeQuery(id+"F26.opExtrude","CAP_EDGE",EDGE,{"disambiguationData":[OSD([sQuery(id+"F25.wireOp",EDGE,"E45.3")])],"isStart":false});
            var Q1;
            Q1=makeQuery(id+"F26.opExtrude","CAP_EDGE",EDGE,{"disambiguationData":[OSD([sQuery(id+"F25.wireOp",EDGE,"E45.2")])],"isStart":false});
            var Q2;
            Q2=makeQuery(id+"F26.opExtrude","CAP_EDGE",EDGE,{"disambiguationData":[OSD([sQuery(id+"F25.wireOp",EDGE,"E45.1")])],"isStart":false});
            var Q3;
            Q3=makeQuery(id+"F26.opExtrude","CAP_EDGE",EDGE,{"disambiguationData":[OSD([sQuery(id+"F25.wireOp",EDGE,"E45.0")])],"isStart":false});
            var Q4;
            Q4=makeQuery(id+"F26.opExtrude","CAP_EDGE",EDGE,{"disambiguationData":[OSD([sQuery(id+"F25.wireOp",EDGE,"E45.5")])],"isStart":false});
            var Q5;
            Q5=makeQuery(id+"F26.opExtrude","CAP_EDGE",EDGE,{"disambiguationData":[OSD([sQuery(id+"F25.wireOp",EDGE,"E45.4")])],"isStart":false});
            var Q6;
            Q6=makeQuery(id+"F26.opExtrude","CAP_EDGE",EDGE,{"disambiguationData":[OSD([sQuery(id+"F25.wireOp",EDGE,"E45.4")])],"isStart":true});
            var Q7;
            Q7=makeQuery(id+"F26.opExtrude","CAP_EDGE",EDGE,{"disambiguationData":[OSD([sQuery(id+"F25.wireOp",EDGE,"E45.3")])],"isStart":true});
            var Q8;
            Q8=makeQuery(id+"F26.opExtrude","CAP_EDGE",EDGE,{"disambiguationData":[OSD([sQuery(id+"F25.wireOp",EDGE,"E45.2")])],"isStart":true});
            var Q9;
            Q9=makeQuery(id+"F26.opExtrude","CAP_EDGE",EDGE,{"disambiguationData":[OSD([sQuery(id+"F25.wireOp",EDGE,"E45.5")])],"isStart":true});
            var Q10;
            Q10=makeQuery(id+"F26.opExtrude","CAP_EDGE",EDGE,{"disambiguationData":[OSD([sQuery(id+"F25.wireOp",EDGE,"E45.0")])],"isStart":true});
            var Q11;
            Q11=makeQuery(id+"F26.opExtrude","CAP_EDGE",EDGE,{"disambiguationData":[OSD([sQuery(id+"F25.wireOp",EDGE,"E45.1")])],"isStart":true});
            fillet(context, id + "F29", {"entities" : qUnion([Q0, Q1, Q2, Q3, Q4, Q5, Q6, Q7, Q8, Q9, Q10, Q11]), "radius" : 1 * mm, "tangentPropagation" : true, "allowEdgeOverflow" : false});
        }
        {
            var Q0;
            Q0=qCreatedBy(makeId("Top.planeOp"),FACE);
            var sketch = newSketch(context, id + "F30", { "sketchPlane" : qUnion([Q0])});
            skCircle(sketch, "E48", {"center": v(-75, 0) * mm, "radius": 5.75 * mm});
            skSolve(sketch);
        }
        {
            var Q0;
            Q0 = qSketchRegion(id + "F30", true);
            extrude(context, id + "F31", {"entities" : qUnion([Q0]), "depth" : 1 * mm});
        }
        {
            var Q0;
            Q0=makeQuery(id+"F31.opExtrude","CAP_FACE",FACE,{"disambiguationData":[OSD([sQuery(id+"F30.wireOp",EDGE,"E48")])],"isStart":false});
            var sketch = newSketch(context, id + "F32", { "sketchPlane" : qUnion([Q0])});
            skCircle(sketch, "E49", {"center": v(-75, 0) * mm, "radius": 5 * mm});
            skSolve(sketch);
        }
        {
            var Q0;
            Q0 = qSketchRegion(id + "F32", true);
            extrude(context, id + "F33", {"entities" : qUnion([Q0]), "operationType" : NewBodyOperationType.ADD, "depth" : 3 * mm});
        }
        {
            var Q0;
            Q0=makeQuery(id+"F33.opExtrude","CAP_FACE",FACE,{"disambiguationData":[OSD([sQuery(id+"F32.wireOp",EDGE,"E49")])],"isStart":false});
            var sketch = newSketch(context, id + "F34", { "sketchPlane" : qUnion([Q0])});
            skCircle(sketch, "E50", {"center": v(-75, 0) * mm, "radius": 1.5 * mm});
            skSolve(sketch);
        }
        {
            var Q0;
            Q0 = qSketchRegion(id + "F34", true);
            extrude(context, id + "F35", {"entities" : qUnion([Q0]), "operationType" : NewBodyOperationType.REMOVE, "oppositeDirection" : true, "depth" : 4 * mm});
        }
        {
            var Q0;
            Q0=qCreatedBy(makeId("Top.planeOp"),FACE);
            var sketch = newSketch(context, id + "F36", { "sketchPlane" : qUnion([Q0])});
            skCircle(sketch, "E51", {"center": v(60, 0) * mm, "radius": 8 * mm});
            skSolve(sketch);
        }
        {
            var Q0;
            Q0 = qSketchRegion(id + "F36", true);
            extrude(context, id + "F37", {"entities" : qUnion([Q0]), "depth" : 5 * mm});
        }
        {
            var Q0;
            Q0=makeQuery(id+"F37.opExtrude","CAP_FACE",FACE,{"disambiguationData":[OSD([sQuery(id+"F36.wireOp",EDGE,"E51")])],"isStart":false});
            var sketch = newSketch(context, id + "F38", { "sketchPlane" : qUnion([Q0])});
            skCircle(sketch, "E52", {"center": v(60, 0) * mm, "radius": 2.5 * mm});
            skSolve(sketch);
        }
        {
            var Q0;
            Q0 = qSketchRegion(id + "F38", true);
            extrude(context, id + "F39", {"entities" : qUnion([Q0]), "operationType" : NewBodyOperationType.REMOVE, "oppositeDirection" : true, "depth" : 5 * mm});
        }
        {
            var Q0;
            Q0=qCreatedBy(makeId("Top.planeOp"),FACE);
            var sketch = newSketch(context, id + "F40", { "sketchPlane" : qUnion([Q0])});
            skCircle(sketch, "E53", {"center": v(85, 0) * mm, "radius": 4 * mm});
            skSolve(sketch);
        }
        {
            var Q0;
            Q0 = qSketchRegion(id + "F40", true);
            extrude(context, id + "F41", {"entities" : qUnion([Q0]), "depth" : 185 * mm});
        }
    });
